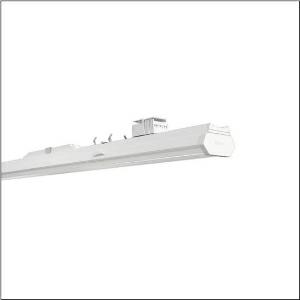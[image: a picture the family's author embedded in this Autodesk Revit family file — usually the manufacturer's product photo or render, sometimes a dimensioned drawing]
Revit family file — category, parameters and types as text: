
# Revit family: licross_r__11_protected_mo_51tp12dn49xf3s4_e03f
name_source: partatom
category: Lighting Fixtures
units: mm (PartAtom-declared; Revit-internal decimal feet)

## family parameters
Cut with Voids When Loaded = No
Host = Face
Light Source = No
Part Type = Normal
Room Calculation Point = No
Round Connector Dimension = Use Diameter
Shared = No

## types (1)
- --- (1 x LED, 9020 lm, 60 W, 4000K)
    Apparent Load = 60 VA
    CIE Flux Codes = 73 92 98 99 100
    Color Rendering = 80
    Color Temperature = 4000K
    Default Elevation = 1800 mm
    Description = Licross® 11 Protected MO, luminaire insert, of sheet steel, galvanised, coil coated, white, length: 1.500mm, width: 90mm, height: 101mm, LED rated luminous flux: 9.020lm, light colour: 840, control gear: DALI 2, control gear: ECG DALI, with plug, 6-pole, with phase selection, for trunking rail, 9 or 11-core, mains connection: 220..240V, AC/DC, 0/50..60Hz, halogen-free wiring, for emergency light function, converter,control gear: single battery element, battery: LiFeP04, 9Ah, primary optical cover: cover, of PMMA, light emission: direct with ceiling illumination distribution, primary light characteristic: symmetric, protection rating (complete): IP64, insulation class (complete): insulation class I (protective earthing), certification: CE, UKCA, protection symbol: D if used in an environment with conductive dust loads with corresponding accessories, permissible ambient temperature for indoor applications: +5..+35°C, standard: EN 60598-2-22, corresponds to IFS (International Featured Standards) requirements for safety and quality in the food industry, reducing of maximum allowable ambient temperature of 5°C with ceiling mounting, LABS conformity tested according to VDMA 24364:2018-05, packaging unit: 1 piece
    Height = 92 mm
    Lamp = 1 x LED
    Lamp Light Flux = 9020 lm
    Lamp Power = 60 W
    Lamp count = 1
    Length = 1500 mm
    Luminous efficacy = 150 lm/W
    Manufacturer = Siteco
    ModVariant = No
    Model = 51TP12DN49XF3S4
    Mounting Place = Ceiling
    Mounting Type = Pendant
    Number of Poles = 1
    OnlyDefault = Yes
    Power Factor = 1
    Product Name = Licross® 11 Protected MO
    Product group = luminaire insert
    ProductGroupID = 902
    Protection Class = Protection class I
    Protection Degree = IP 64
    RLX_Detail_Level = 1
    RlxData = <blob elided: 24733 chars, md5=f1faaa11>
    Socket = socket
    Standby Power = 0 W
    System Light Flux = 9020 lm
    System Power = 60 W
    Type Comments = : AC-mode, luminous flux: 100 % | dim-lin: 254 | 370 mA
    Type Image = l_1256148.jpg
    URL = http://relux.com
    VarID = @adj_115651
    Voltage = 0 V
    Weight = 0.00 kg
    Width = 88 mm

## geometry (parser evidence)
native form markers: Blend x4, Sweep x12
no freeform markers — native parametric forms only
